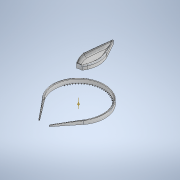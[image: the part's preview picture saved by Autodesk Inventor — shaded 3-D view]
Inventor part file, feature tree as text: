
AUTODESK INVENTOR PART (.ipt)
format: ipt  version: 2022 (Build 260153000, 153)  size: 1,850,368 bytes
history: native  units: in
note: dims shown in document units (in); Inventor stores cm internally (conversion verified against a paired STEP export)
features: fillet x14, extrude x8, sketch x7, other x1, pattern_circular x1
ambient origin geometry x8: Origin, YZ Plane, XZ Plane, XY Plane, X Axis, Y Axis, Z Axis, Center Point
bodies: Solid1 (feature_tree), Solid2 (feature_tree)
feature tree (31):
  extrude  "Extrusion1"  TaperAngle=0.0deg  [1 undecoded]
  extrude  "Extrusion2"  Depth=2.2638in
  fillet  "Fillet2"  Radius=0.1181in
  other  "Work Axis1"
  pattern_circular  "Circular Pattern1"  [2 undecoded]
  extrude  "Extrusion3"  Depth=2.1102in
  extrude  "Extrusion4"  Depth=11.811in
  fillet  "Fillet5"  Radius=0.889in
  fillet  "Fillet6"  Radius=3.1496in
  fillet  "Fillet7"  Radius=0.0394in
  fillet  "Fillet8"  Radius=0.0118in
  fillet  "Fillet19"  Radius=0.0427in
  extrude  "Extrusion5"  Depth=59.0551in
  extrude  "Extrusion7"  Depth=59.0551in
  extrude  "Extrusion6"  Depth=0.3937in TaperAngle=0.0deg
  fillet  "Fillet20"  Radius=0.1181in
  fillet  "Fillet21"  Radius=4.3307in
  fillet  "Fillet22"  Radius=25.1969in
  fillet  "Fillet23"  Radius=0.7087in
  fillet  "Fillet24"  Radius=4.3307in
  fillet  "Fillet25"  Radius=0.3937in
  fillet  "Fillet26"  [1 undecoded]
  extrude  "Extrusion8"  Depth=0.0248in
  fillet  "Fillet27"  Radius=0.0394in
  sketch  "Sketch2"  dims[d18=0.0in d19=0.0in]
  sketch  "Sketch5"  dims[d20=0.0in d23=2.2638in d25=0.1181in]
  sketch  "Sketch6"  dims[d26=0.1181in]
  sketch  "Sketch7"  dims[d27=0.1181in]
  sketch  "Sketch8"  dims[d30=0.3937in d31=0.0in]
  sketch  "Sketch9"  dims[d48=0.0433in d49=0.0in]
  sketch  "Sketch11"  dims[d50=0.0118in d57=0.0787in d58=0.0157in d59=0.7594in d60=2.1102in d61=11.811in d62=-0.962in d64=0.889in d65=3.1496in d68=0.0394in d69=0.0118in d70=0.0427in d71=59.0551in d72=59.0551in d73=0.3937in d74=0.0in d75=0.1181in d76=4.3307in d77=25.1969in d78=0.7087in d79=4.3307in d80=0.3937in d81=0.0in d82=0.0in d85=0.0248in d86=0.0394in d87=0.0394in d88=0.0236in d104=0.3937in d105=0.0in d107=0.315in d108=0.0in d121=0.0591in d122=0.0591in d123=1.378in d125=0.3346in d126=0.0in d130=2.3495in d131=2.2052in d132=2.0826in d133=1.4138in d134=2.5284in d135=1.4901in d136=2.1896in d137=2.5146in d138=2.7368in d139=1.4623in d140=0.488in d141=0.3104in d142=0.2859in d143=0.2088in d144=0.2171in d145=0.23in d147=0.2362in d148=0.0787in d149=0.0787in d150=0.0394in d153=0.0394in d154=0.1181in d155=0.0787in d156=0.0787in d158=23.622in d159=1.9685in d161=7.8078in d162=2.3622in d163=0.7874in d164=0.9817in d165=0.0in d166=0.0in d167=0.0787in d168=0.1969in d169=0.1969in d170=0.1181in d171=0.0197in d172=0.0079in d173=0.0394in d174=0.0197in d175=0.0197in d182=0.0984in d183=0.0394in d184=0.0984in d185=0.0394in d186=0.0591in d187=0.0394in d188=0.0197in d189=0.076in d190=0.0in d191=0.0in d192=0.0079in]
note: 4 required parameter values undecoded (feature->parameter linkage not recoverable at this tier; creation-order binding heuristic only, values carry confidence <= 0.55)
